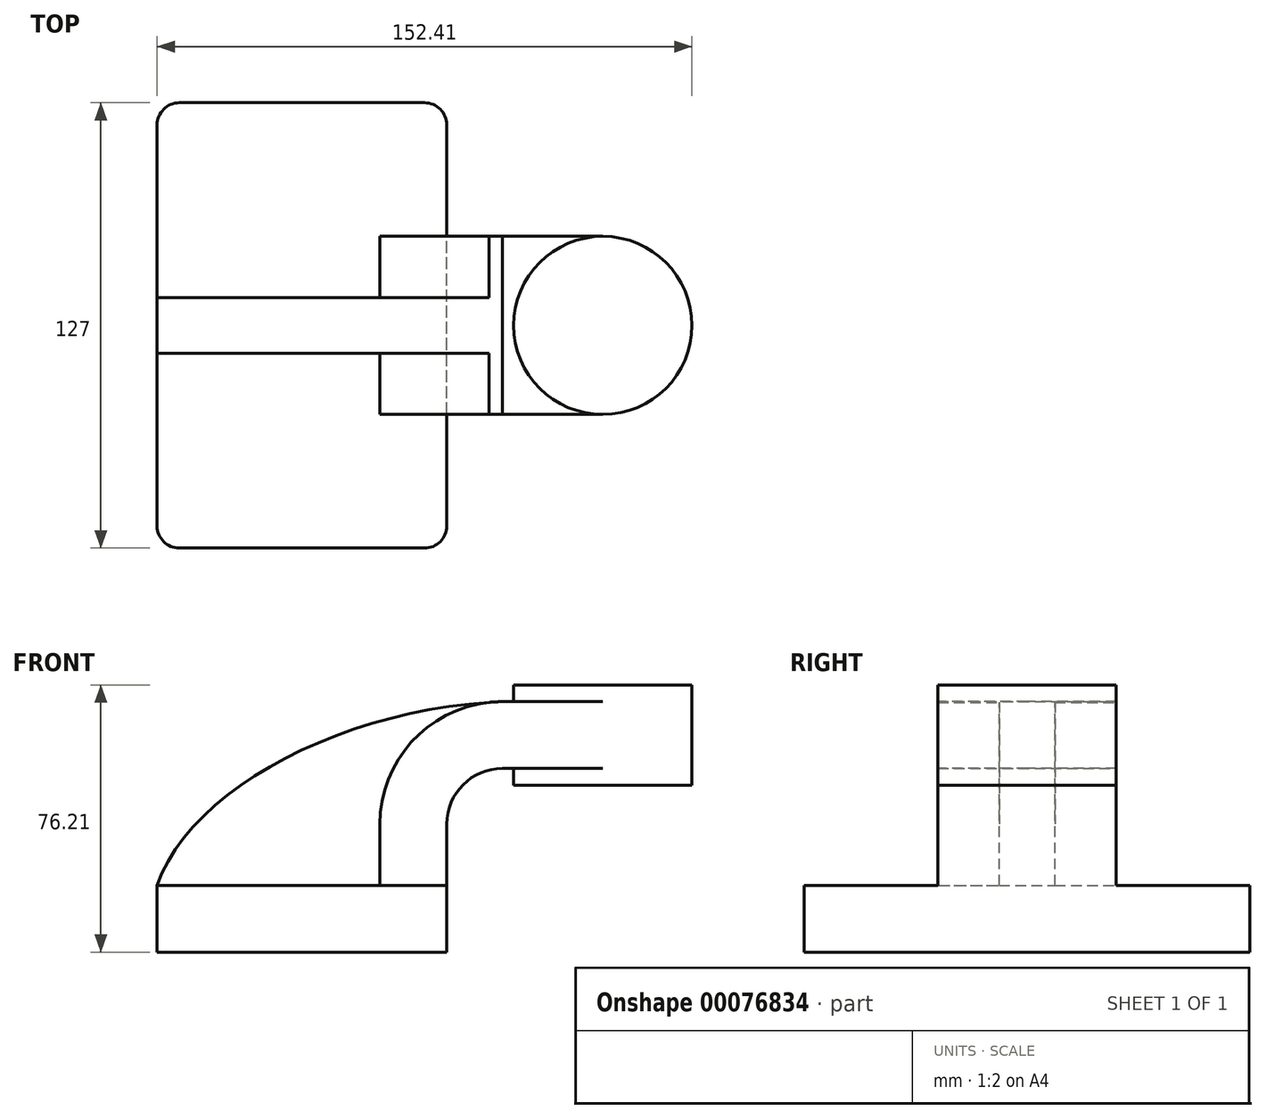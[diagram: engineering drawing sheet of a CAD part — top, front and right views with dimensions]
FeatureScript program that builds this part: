
annotation { "Feature Type Name" : "Feature", "Feature Type Description" : "" }
export const myFeature = defineFeature(function(context is Context, id is Id, definition is map)
    precondition{}
    {
        {
            var Q0;
            Q0=qCreatedBy(makeId("Front.planeOp"),FACE);
            var sketch = newSketch(context, id + "F0", { "sketchPlane" : qUnion([Q0])});
            skLineSegment(sketch, "E0.bottom", {"start": v(41.28, -9.52) * mm, "end": v(-41.27, -9.52) * mm});
            skLineSegment(sketch, "E0.top", {"start": v(41.27, 9.53) * mm, "end": v(-41.28, 9.53) * mm});
            skLineSegment(sketch, "E0.left", {"start": v(41.28, -9.52) * mm, "end": v(41.28, 9.53) * mm});
            skLineSegment(sketch, "E0.right", {"start": v(-41.27, -9.52) * mm, "end": v(-41.28, 9.53) * mm});
            skPoint(sketch, "E0.middle", {"position": v(0, 0) * mm});
            skLineSegment(sketch, "E1.bottom", {"start": v(60.32, 38.1) * mm, "end": v(111.12, 38.1) * mm});
            skLineSegment(sketch, "E1.top", {"start": v(60.32, 66.68) * mm, "end": v(111.12, 66.68) * mm});
            skLineSegment(sketch, "E1.left", {"start": v(60.32, 38.1) * mm, "end": v(60.32, 66.68) * mm});
            skLineSegment(sketch, "E1.right", {"start": v(111.13, 38.1) * mm, "end": v(111.12, 66.68) * mm});
            skPoint(sketch, "E1.middle", {"position": v(85.72, 52.39) * mm});
            skLineSegment(sketch, "E2", {"start": v(41.27, 9.53) * mm, "end": v(41.27, 26.99) * mm});
            skArc(sketch, "E3", {"start": v(41.27, 26.99) * mm, "mid": v(45.92, 38.21) * mm, "end": v(57.15, 42.86) * mm});
            skLineSegment(sketch, "E4", {"start": v(57.15, 42.86) * mm, "end": v(85.73, 42.86) * mm});
            skLineSegment(sketch, "E5.0", {"start": v(57.15, 61.91) * mm, "end": v(85.73, 61.91) * mm});
            skArc(sketch, "E5.1", {"start": v(22.23, 26.99) * mm, "mid": v(32.45, 51.68) * mm, "end": v(57.15, 61.91) * mm});
            skLineSegment(sketch, "E5.2", {"start": v(22.22, 9.53) * mm, "end": v(22.22, 26.99) * mm});
            skLineSegment(sketch, "E6", {"start": v(85.73, 38.1) * mm, "end": v(85.73, 66.68) * mm});
            skFitSpline(sketch, "E7", {"points": [v(-41.28, 9.53) * mm, v(57.15, 61.91) * mm], "startDerivative": vector(28.66, 82.49) * mm, "endDerivative": vector(136.75, 5.71) * mm});
            skSolve(sketch);
        }
        {
            var Q0;
            Q0=makeQuery(id+"F0.imprint","IMPRINT",FACE,{"disambiguationData":[TD([[makeQuery(id+"F0.imprint","IMPRINT",EDGE,{"derivedFrom":sQuery(id+"F0.wireOp",EDGE,"E0.bottom")}),-1.0]])]});
            extrude(context, id + "F1", {"entities" : qUnion([Q0]), "endBound" : BoundingType.SYMMETRIC, "depth" : 127 * mm});
        }
        {
            var Q0;
            {var subQ1=sQuery(id+"F0.wireOp",EDGE,"E2");Q0=makeQuery(id+"F0.imprint","IMPRINT",FACE,{"disambiguationData":[TD([[makeQuery(id+"F0.imprint","IMPRINT",EDGE,{"derivedFrom":subQ1}),1.0]])]});}
            var Q1;
            {var subQ0=sQuery(id+"F0.wireOp",EDGE,"E4");var subQ1=sQuery(id+"F0.wireOp",EDGE,"E1.left");var subQ2=makeQuery(id+"F0.imprint","INTERSECT",VERTEX,{"derivedFrom":[subQ1,subQ0]});Q1=makeQuery(id+"F0.imprint","IMPRINT",FACE,{"disambiguationData":[TD([[makeQuery(id+"F0.imprint","IMPRINT",EDGE,{"disambiguationData":[TD([[subQ2,-1.0]])],"derivedFrom":subQ1}),-1.0]])]});}
            extrude(context, id + "F2", {"entities" : qUnion([Q0, Q1]), "operationType" : NewBodyOperationType.ADD, "endBound" : BoundingType.SYMMETRIC, "depth" : 50.8 * mm});
        }
        {
            var Q0;
            {var subQ3=sQuery(id+"F0.wireOp",EDGE,"E5.2");Q0=makeQuery(id+"F0.imprint","IMPRINT",FACE,{"disambiguationData":[TD([[makeQuery(id+"F0.imprint","IMPRINT",EDGE,{"derivedFrom":subQ3}),1.0]])]});}
            extrude(context, id + "F3", {"entities" : qUnion([Q0]), "operationType" : NewBodyOperationType.ADD, "endBound" : BoundingType.SYMMETRIC, "depth" : 15.88 * mm});
        }
        {
            var Q0;
            {var subQ0=sQuery(id+"F0.wireOp",EDGE,"E1.right");Q0=makeQuery(id+"F0.imprint","IMPRINT",FACE,{"disambiguationData":[TD([[makeQuery(id+"F0.imprint","IMPRINT",EDGE,{"derivedFrom":subQ0}),1.0]])]});}
            var Q1;
            Q1=sQuery(id+"F0.wireOp",EDGE,"E6");
            revolve(context, id + "F4", {"operationType" : NewBodyOperationType.ADD, "entities" : qUnion([Q0]), "axis" : qUnion([Q1]), "revolveType" : RevolveType.FULL});
        }
        {
            var Q0;
            Q0=makeQuery(id+"F1.opExtrude","CAP_EDGE",EDGE,{"disambiguationData":[OSD([sQuery(id+"F0.wireOp",EDGE,"E0.right")])],"isStart":false});
            var Q1;
            Q1=makeQuery(id+"F1.opExtrude","CAP_EDGE",EDGE,{"disambiguationData":[OSD([sQuery(id+"F0.wireOp",EDGE,"E0.left")])],"isStart":false});
            var Q2;
            Q2=makeQuery(id+"F1.opExtrude","CAP_EDGE",EDGE,{"disambiguationData":[OSD([sQuery(id+"F0.wireOp",EDGE,"E0.left")])],"isStart":true});
            var Q3;
            Q3=makeQuery(id+"F1.opExtrude","CAP_EDGE",EDGE,{"disambiguationData":[OSD([sQuery(id+"F0.wireOp",EDGE,"E0.right")])],"isStart":true});
            fillet(context, id + "F5", {"entities" : qUnion([Q0, Q1, Q2, Q3]), "radius" : 6.35 * mm, "tangentPropagation" : true, "allowEdgeOverflow" : false});
        }
    });
